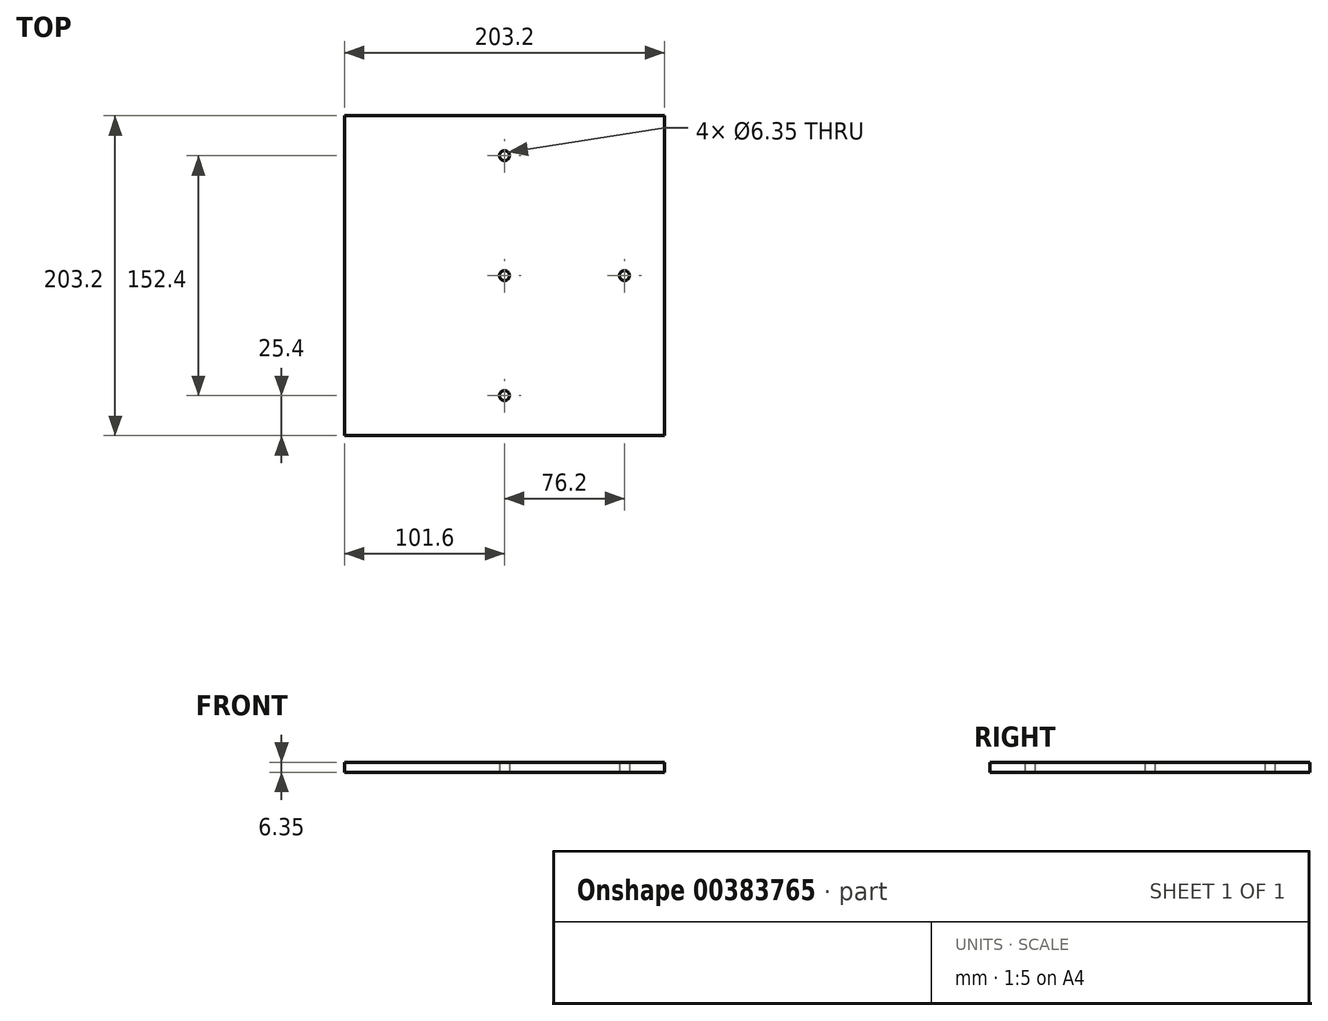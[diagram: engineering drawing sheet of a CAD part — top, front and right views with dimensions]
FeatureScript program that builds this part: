
annotation { "Feature Type Name" : "Feature", "Feature Type Description" : "" }
export const myFeature = defineFeature(function(context is Context, id is Id, definition is map)
    precondition{}
    {
        {
            var Q0;
            Q0=qCreatedBy(makeId("Top.planeOp"),FACE);
            var sketch = newSketch(context, id + "F0", { "sketchPlane" : qUnion([Q0])});
            skLineSegment(sketch, "E0.bottom", {"start": v(0, 0) * mm, "end": v(203.2, 0) * mm});
            skLineSegment(sketch, "E0.top", {"start": v(0, 203.2) * mm, "end": v(203.2, 203.2) * mm});
            skLineSegment(sketch, "E0.left", {"start": v(0, 0) * mm, "end": v(0, 203.2) * mm});
            skLineSegment(sketch, "E0.right", {"start": v(203.2, 0) * mm, "end": v(203.2, 203.2) * mm});
            skCircle(sketch, "E1", {"center": v(101.6, 177.8) * mm, "radius": 3.18 * mm});
            skCircle(sketch, "E2", {"center": v(101.6, 101.6) * mm, "radius": 3.18 * mm});
            skCircle(sketch, "E3", {"center": v(177.8, 101.6) * mm, "radius": 3.18 * mm});
            skCircle(sketch, "E4", {"center": v(101.6, 25.4) * mm, "radius": 3.18 * mm});
            skSolve(sketch);
        }
        {
            var Q0;
            Q0=makeQuery(id+"F0.imprint","IMPRINT",FACE,{"disambiguationData":[TD([[makeQuery(id+"F0.imprint","IMPRINT",EDGE,{"derivedFrom":sQuery(id+"F0.wireOp",EDGE,"E0.bottom")}),1.0]])]});
            extrude(context, id + "F1", {"entities" : qUnion([Q0]), "depth" : 6.35 * mm});
        }
    });
